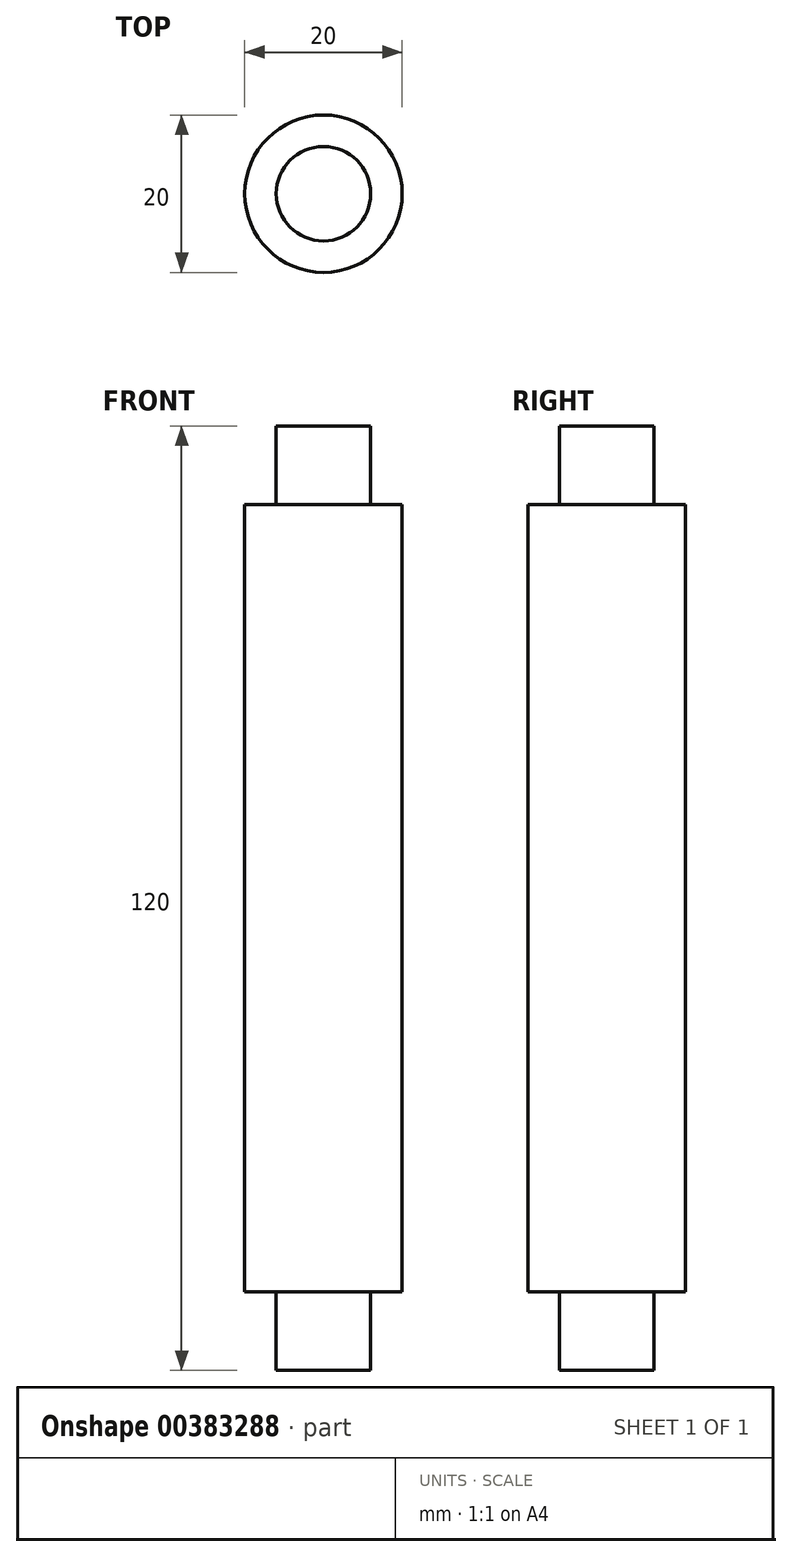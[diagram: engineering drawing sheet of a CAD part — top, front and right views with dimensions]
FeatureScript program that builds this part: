
annotation { "Feature Type Name" : "Feature", "Feature Type Description" : "" }
export const myFeature = defineFeature(function(context is Context, id is Id, definition is map)
    precondition{}
    {
        {
            var Q0;
            Q0=qCreatedBy(makeId("Right.planeOp"),FACE);
            var sketch = newSketch(context, id + "F0", { "sketchPlane" : qUnion([Q0])});
            skLineSegment(sketch, "E0", {"start": v(0, 0) * mm, "end": v(0, 120) * mm, "construction": true});
            skLineSegment(sketch, "E1.bottom", {"start": v(0, 0) * mm, "end": v(6, 0) * mm});
            skLineSegment(sketch, "E1.top", {"start": v(0, 10) * mm, "end": v(6, 10) * mm});
            skLineSegment(sketch, "E1.left", {"start": v(0, 0) * mm, "end": v(0, 10) * mm});
            skLineSegment(sketch, "E1.right", {"start": v(6, 0) * mm, "end": v(6, 10) * mm});
            skLineSegment(sketch, "E2.bottom", {"start": v(0, 10) * mm, "end": v(10, 10) * mm});
            skLineSegment(sketch, "E2.top", {"start": v(0, 110) * mm, "end": v(10, 110) * mm});
            skLineSegment(sketch, "E2.left", {"start": v(0, 10) * mm, "end": v(0, 110) * mm});
            skLineSegment(sketch, "E2.right", {"start": v(10, 10) * mm, "end": v(10, 110) * mm});
            skLineSegment(sketch, "E3.bottom", {"start": v(0, 120) * mm, "end": v(6, 120) * mm});
            skLineSegment(sketch, "E3.top", {"start": v(0, 110) * mm, "end": v(6, 110) * mm});
            skLineSegment(sketch, "E3.left", {"start": v(0, 120) * mm, "end": v(0, 110) * mm});
            skLineSegment(sketch, "E3.right", {"start": v(6, 120) * mm, "end": v(6, 110) * mm});
            skSolve(sketch);
        }
        {
            var Q0;
            Q0=makeQuery(id+"F0.imprint","IMPRINT",FACE,{"disambiguationData":[TD([[makeQuery(id+"F0.imprint","IMPRINT",EDGE,{"derivedFrom":sQuery(id+"F0.wireOp",EDGE,"E2.top")}),-1.0]])]});
            var Q1;
            Q1=makeQuery(id+"F0.imprint","IMPRINT",FACE,{"disambiguationData":[TD([[makeQuery(id+"F0.imprint","IMPRINT",EDGE,{"derivedFrom":sQuery(id+"F0.wireOp",EDGE,"E3.bottom")}),-1.0]])]});
            var Q2;
            Q2=makeQuery(id+"F0.imprint","IMPRINT",FACE,{"disambiguationData":[TD([[makeQuery(id+"F0.imprint","IMPRINT",EDGE,{"derivedFrom":sQuery(id+"F0.wireOp",EDGE,"E1.bottom")}),1.0]])]});
            var Q3;
            Q3=sQuery(id+"F0.wireOp",EDGE,"E2.left");
            revolve(context, id + "F1", {"entities" : qUnion([Q0, Q1, Q2]), "axis" : qUnion([Q3]), "revolveType" : RevolveType.FULL});
        }
    });
